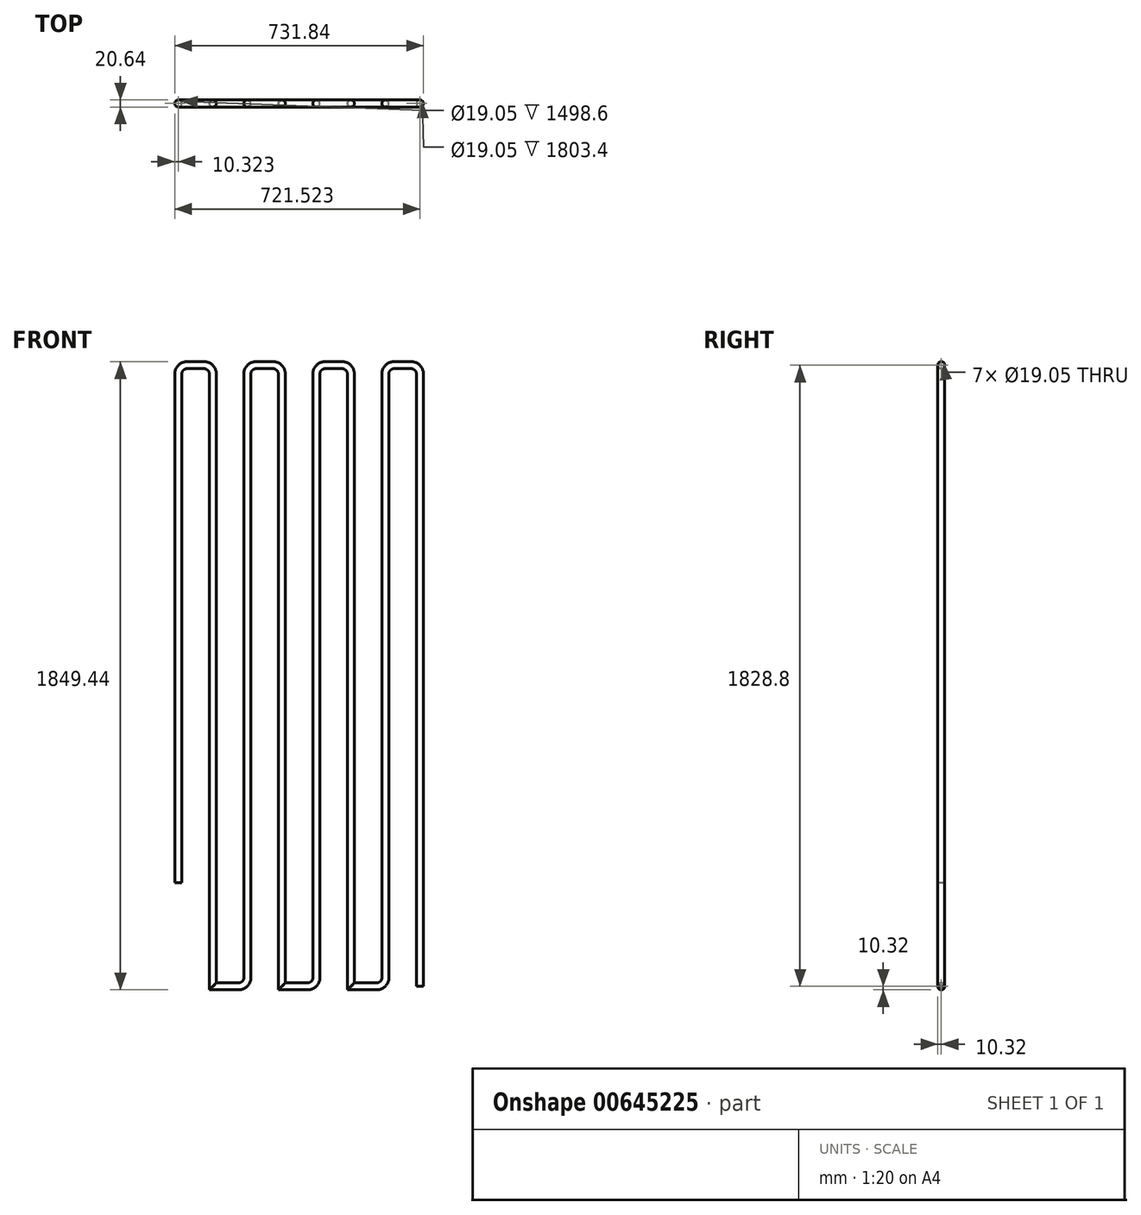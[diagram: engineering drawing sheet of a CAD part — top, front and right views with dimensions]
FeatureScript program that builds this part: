
annotation { "Feature Type Name" : "Feature", "Feature Type Description" : "" }
export const myFeature = defineFeature(function(context is Context, id is Id, definition is map)
    precondition{}
    {
        {
            var Q0;
            Q0=qCreatedBy(makeId("Front.planeOp"),FACE);
            var sketch = newSketch(context, id + "F0", { "sketchPlane" : qUnion([Q0])});
            skLineSegment(sketch, "E0", {"start": v(-936.29, -737.58) * mm, "end": v(-936.29, 761.02) * mm});
            skLineSegment(sketch, "E1", {"start": v(-910.89, 786.42) * mm, "end": v(-860.09, 786.42) * mm});
            skLineSegment(sketch, "E2", {"start": v(-834.69, 761.02) * mm, "end": v(-834.69, -1042.38) * mm});
            skLineSegment(sketch, "E3", {"start": v(-834.69, -1042.38) * mm, "end": v(-758.49, -1042.38) * mm});
            skLineSegment(sketch, "E4", {"start": v(-733.09, -1016.98) * mm, "end": v(-733.09, 761.02) * mm});
            skLineSegment(sketch, "E5", {"start": v(-707.69, 786.42) * mm, "end": v(-656.89, 786.42) * mm});
            skLineSegment(sketch, "E6", {"start": v(-631.49, 761.02) * mm, "end": v(-631.49, -1042.38) * mm});
            skLineSegment(sketch, "E7", {"start": v(-631.49, -1042.38) * mm, "end": v(-555.29, -1042.38) * mm});
            skLineSegment(sketch, "E8", {"start": v(-529.89, -1016.98) * mm, "end": v(-529.89, 761.02) * mm});
            skLineSegment(sketch, "E9", {"start": v(-504.49, 786.42) * mm, "end": v(-453.69, 786.42) * mm});
            skLineSegment(sketch, "E10", {"start": v(-428.29, 761.02) * mm, "end": v(-428.29, -1042.38) * mm});
            skLineSegment(sketch, "E11", {"start": v(-428.29, -1042.38) * mm, "end": v(-352.09, -1042.38) * mm});
            skLineSegment(sketch, "E12", {"start": v(-326.69, -1016.98) * mm, "end": v(-326.69, 761.02) * mm});
            skLineSegment(sketch, "E13", {"start": v(-301.29, 786.42) * mm, "end": v(-250.49, 786.42) * mm});
            skLineSegment(sketch, "E14", {"start": v(-225.09, 761.02) * mm, "end": v(-225.09, -1042.38) * mm});
            skPoint(sketch, "E15.visualSharp", {"position": v(-936.29, 786.42) * mm});
            skArc(sketch, "E15.filletArc", {"start": v(-910.89, 786.42) * mm, "mid": v(-928.85, 778.98) * mm, "end": v(-936.29, 761.02) * mm});
            skPoint(sketch, "E16.visualSharp", {"position": v(-834.69, 786.42) * mm});
            skArc(sketch, "E16.filletArc", {"start": v(-834.69, 761.02) * mm, "mid": v(-842.13, 778.98) * mm, "end": v(-860.09, 786.42) * mm});
            skPoint(sketch, "E17.visualSharp", {"position": v(-733.09, 786.42) * mm});
            skArc(sketch, "E17.filletArc", {"start": v(-707.69, 786.42) * mm, "mid": v(-725.65, 778.98) * mm, "end": v(-733.09, 761.02) * mm});
            skPoint(sketch, "E18.visualSharp", {"position": v(-631.49, 786.42) * mm});
            skArc(sketch, "E18.filletArc", {"start": v(-631.49, 761.02) * mm, "mid": v(-638.93, 778.98) * mm, "end": v(-656.89, 786.42) * mm});
            skPoint(sketch, "E19.visualSharp", {"position": v(-529.89, 786.42) * mm});
            skArc(sketch, "E19.filletArc", {"start": v(-504.49, 786.42) * mm, "mid": v(-522.45, 778.98) * mm, "end": v(-529.89, 761.02) * mm});
            skPoint(sketch, "E20.visualSharp", {"position": v(-428.29, 786.42) * mm});
            skArc(sketch, "E20.filletArc", {"start": v(-428.29, 761.02) * mm, "mid": v(-435.73, 778.98) * mm, "end": v(-453.69, 786.42) * mm});
            skPoint(sketch, "E21.visualSharp", {"position": v(-326.69, 786.42) * mm});
            skArc(sketch, "E21.filletArc", {"start": v(-301.29, 786.42) * mm, "mid": v(-319.25, 778.98) * mm, "end": v(-326.69, 761.02) * mm});
            skPoint(sketch, "E22.visualSharp", {"position": v(-225.09, 786.42) * mm});
            skArc(sketch, "E22.filletArc", {"start": v(-225.09, 761.02) * mm, "mid": v(-232.53, 778.98) * mm, "end": v(-250.49, 786.42) * mm});
            skPoint(sketch, "E23.visualSharp", {"position": v(-733.09, -1042.38) * mm});
            skArc(sketch, "E23.filletArc", {"start": v(-758.49, -1042.38) * mm, "mid": v(-740.53, -1034.94) * mm, "end": v(-733.09, -1016.98) * mm});
            skPoint(sketch, "E24.visualSharp", {"position": v(-529.89, -1042.38) * mm});
            skArc(sketch, "E24.filletArc", {"start": v(-555.29, -1042.38) * mm, "mid": v(-537.33, -1034.94) * mm, "end": v(-529.89, -1016.98) * mm});
            skPoint(sketch, "E25.visualSharp", {"position": v(-326.69, -1042.38) * mm});
            skArc(sketch, "E25.filletArc", {"start": v(-352.09, -1042.38) * mm, "mid": v(-334.13, -1034.94) * mm, "end": v(-326.69, -1016.98) * mm});
            skLineSegment(sketch, "E26", {"start": v(-834.69, -1042.38) * mm, "end": v(-834.69, -1194.78) * mm});
            skLineSegment(sketch, "E27", {"start": v(-631.49, -1042.38) * mm, "end": v(-631.49, -1194.78) * mm});
            skLineSegment(sketch, "E28", {"start": v(-428.29, -1042.38) * mm, "end": v(-428.29, -1194.78) * mm});
            skLineSegment(sketch, "E29", {"start": v(-225.09, -1042.38) * mm, "end": v(-225.09, -1194.78) * mm});
            skLineSegment(sketch, "E30", {"start": v(-936.29, -737.58) * mm, "end": v(-1139.49, -737.58) * mm});
            skLineSegment(sketch, "E31", {"start": v(-936.29, -737.58) * mm, "end": v(-936.29, -1194.78) * mm});
            skLineSegment(sketch, "E32", {"start": v(-235.07, -737.58) * mm, "end": v(-31.87, -737.58) * mm});
            skSolve(sketch);
        }
        {
            var Q0;
            Q0=qCreatedBy(makeId("Top.planeOp"),FACE);
            var Q1;
            Q1=sQuery(id+"F0.wireOp",VERTEX,"E0.start");
            cPlane(context, id + "F1", {"entities" : qUnion([Q0, Q1]), "cplaneType" : CPlaneType.PLANE_POINT, "offset" : 1277.62 * mm, "oppositeDirection" : true, "width" : 152.4 * mm, "height" : 152.4 * mm});
        }
        {
            var Q0;
            Q0=qCreatedBy(id+"F1.planeOp",FACE);
            var sketch = newSketch(context, id + "F2", { "sketchPlane" : qUnion([Q0])});
            skCircle(sketch, "E33", {"center": v(-936.29, 0) * mm, "radius": 9.53 * mm});
            skCircle(sketch, "E34", {"center": v(-936.29, 0) * mm, "radius": 10.32 * mm});
            skSolve(sketch);
        }
        {
            var Q0;
            Q0=makeQuery(id+"F2.imprint","IMPRINT",FACE,{"disambiguationData":[TD([[makeQuery(id+"F2.imprint","IMPRINT",EDGE,{"derivedFrom":sQuery(id+"F2.wireOp",EDGE,"E33")}),-1.0]])]});
            var Q1;
            Q1=sQuery(id+"F0.wireOp",EDGE,"E0");
            var Q2;
            Q2=sQuery(id+"F0.wireOp",EDGE,"E15.filletArc");
            var Q3;
            Q3=sQuery(id+"F0.wireOp",EDGE,"E1");
            var Q4;
            Q4=sQuery(id+"F0.wireOp",EDGE,"E16.filletArc");
            var Q5;
            Q5=sQuery(id+"F0.wireOp",EDGE,"E2");
            var Q6;
            Q6=sQuery(id+"F0.wireOp",EDGE,"E3");
            var Q7;
            Q7=sQuery(id+"F0.wireOp",EDGE,"E23.filletArc");
            var Q8;
            Q8=sQuery(id+"F0.wireOp",EDGE,"E4");
            var Q9;
            Q9=sQuery(id+"F0.wireOp",EDGE,"E12");
            var Q10;
            Q10=sQuery(id+"F0.wireOp",EDGE,"E17.filletArc");
            var Q11;
            Q11=sQuery(id+"F0.wireOp",EDGE,"E9");
            var Q12;
            Q12=sQuery(id+"F0.wireOp",EDGE,"E19.filletArc");
            var Q13;
            Q13=sQuery(id+"F0.wireOp",EDGE,"E5");
            var Q14;
            Q14=sQuery(id+"F0.wireOp",EDGE,"E21.filletArc");
            var Q15;
            Q15=sQuery(id+"F0.wireOp",EDGE,"E20.filletArc");
            var Q16;
            Q16=sQuery(id+"F0.wireOp",EDGE,"E18.filletArc");
            var Q17;
            Q17=sQuery(id+"F0.wireOp",EDGE,"E6");
            var Q18;
            Q18=sQuery(id+"F0.wireOp",EDGE,"E7");
            var Q19;
            Q19=sQuery(id+"F0.wireOp",EDGE,"E24.filletArc");
            var Q20;
            Q20=sQuery(id+"F0.wireOp",EDGE,"E8");
            var Q21;
            Q21=sQuery(id+"F0.wireOp",EDGE,"E10");
            var Q22;
            Q22=sQuery(id+"F0.wireOp",EDGE,"E11");
            var Q23;
            Q23=sQuery(id+"F0.wireOp",EDGE,"E25.filletArc");
            var Q24;
            Q24=sQuery(id+"F0.wireOp",EDGE,"E13");
            var Q25;
            Q25=sQuery(id+"F0.wireOp",EDGE,"E22.filletArc");
            var Q26;
            Q26=sQuery(id+"F0.wireOp",EDGE,"E14");
            sweep(context, id + "F3", {"profiles" : qUnion([Q0]), "path" : qUnion([Q1, Q2, Q3, Q4, Q5, Q6, Q7, Q8, Q9, Q10, Q11, Q12, Q13, Q14, Q15, Q16, Q17, Q18, Q19, Q20, Q21, Q22, Q23, Q24, Q25, Q26])});
        }
    });
